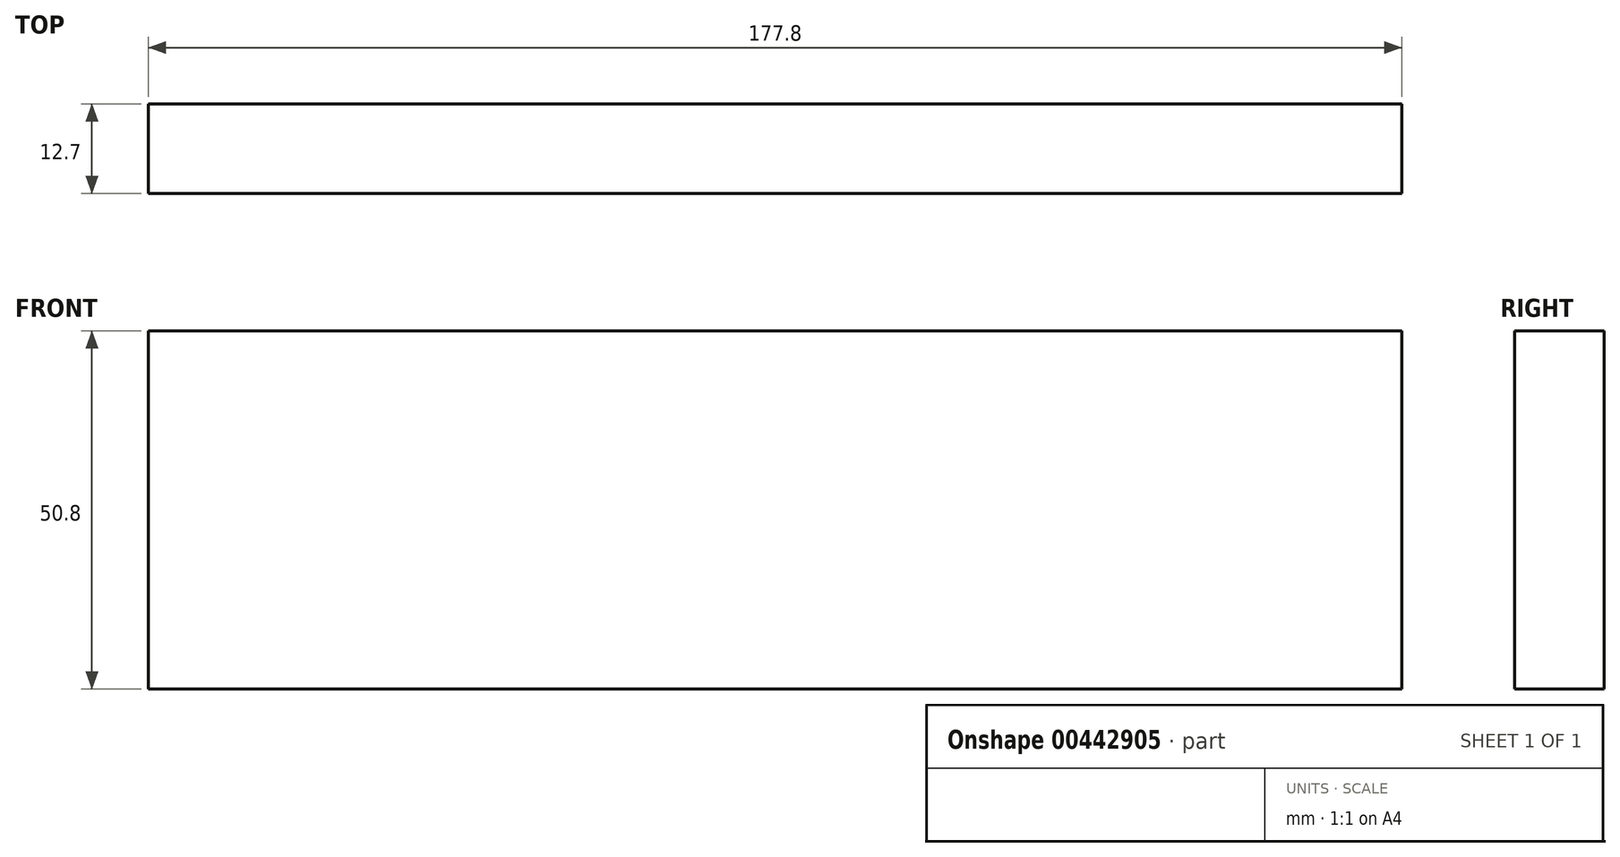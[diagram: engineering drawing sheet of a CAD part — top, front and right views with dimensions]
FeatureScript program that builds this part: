
annotation { "Feature Type Name" : "Feature", "Feature Type Description" : "" }
export const myFeature = defineFeature(function(context is Context, id is Id, definition is map)
    precondition{}
    {
        {
            var Q0;
            Q0=qCreatedBy(makeId("Front.planeOp"),FACE);
            var sketch = newSketch(context, id + "F0", { "sketchPlane" : qUnion([Q0])});
            skLineSegment(sketch, "E0.bottom", {"start": v(88.9, 25.4) * mm, "end": v(-88.9, 25.4) * mm});
            skLineSegment(sketch, "E0.top", {"start": v(88.9, -25.4) * mm, "end": v(-88.9, -25.4) * mm});
            skLineSegment(sketch, "E0.left", {"start": v(88.9, 25.4) * mm, "end": v(88.9, -25.4) * mm});
            skLineSegment(sketch, "E0.right", {"start": v(-88.9, 25.4) * mm, "end": v(-88.9, -25.4) * mm});
            skPoint(sketch, "E0.middle", {"position": v(0, 0) * mm});
            skSolve(sketch);
        }
        {
            var Q0;
            Q0 = qSketchRegion(id + "F0", true);
            extrude(context, id + "F1", {"entities" : qUnion([Q0]), "depth" : 12.7 * mm});
        }
    });
